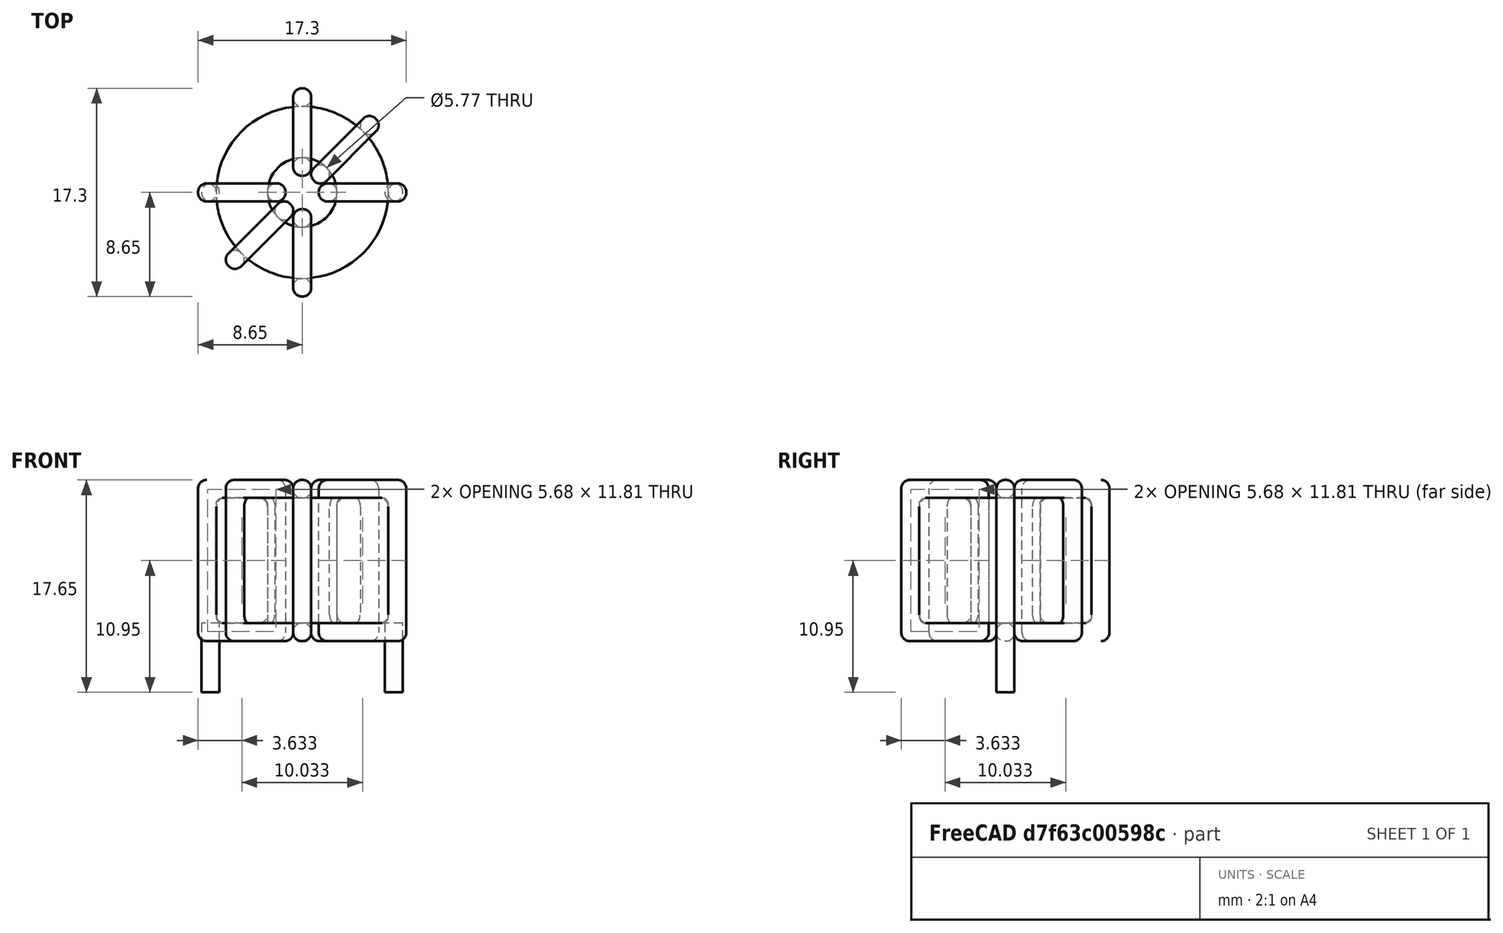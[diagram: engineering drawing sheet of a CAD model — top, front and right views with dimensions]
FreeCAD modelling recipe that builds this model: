
FCSTD DOCUMENT  (FreeCAD 0.16R6703 (Git))
Label: L_Toroid_Horizontal_D17.3mm_P15.24mm_Bourns_2000series
License: All rights reserved
LicenseURL: http://en.wikipedia.org/wiki/All_rights_reserved
objects: Sketcher::SketchObject×6, PartDesign::Pad×6, PartDesign::Fillet×5, Spreadsheet::Sheet×1
note: 23 computed .brp shape members not serialized (recipe doc carries the construction recipe); baked Part::Feature solids carry a one-line shape summary decoded from their .brp

FEATURE [Spreadsheet::Sheet] Spreadsheet  label="dimensions"
  cells = A1=Wx; B1(Wx)=17.3; C1(WW)=5.766666666666667; D1=17.3; A2=Wy; B2(Wy)=17.3; D2=17.3; A3=RM; B3(RMx)=15.24; C3(RMy)=0; A4=d_wire; B4(d_wire)=1.5; A5=H; B5(H)=10.4; A6=offsetx; B6(offsetx)=1.03
FEATURE [Sketcher::SketchObject] Sketch
  Placement = pos=(0,0,2) rot=(0,0,1;0rad)
  expr: Placement.Base.z = 0.5 + Spreadsheet.d_wire
  expr: Constraints[0] = Spreadsheet.Wx / 2 - Spreadsheet.d_wire
  expr: Constraints[4] = Spreadsheet.WW / 2
  expr: Constraints[2] = Spreadsheet.RMy / 2
  expr: Constraints[1] = Spreadsheet.RMx / 2
  sketch-geometry (2):
    g0: Circle CenterX=7.62 CenterY=0 CenterZ=0 NormalX=0 NormalY=0 NormalZ=1 Radius=7.15
    g1: Circle CenterX=7.62 CenterY=0 CenterZ=0 NormalX=0 NormalY=0 NormalZ=1 Radius=2.88333
  constraints (5):
    c: Radius(g0) = 7.15
    c: DistanceX(g-1,g0) = 7.62
    c: DistanceY(g-1,g0) = 0
    c: Coincident(g1,g0)
    c: Radius(g1) = 2.88333
FEATURE [PartDesign::Pad] Pad
  Length = 10.4
  Length2 = 100
  Placement = pos=(0,0,2) rot=(0,0,1;0rad)
  Sketch = -> Sketch
  Type = 0
  expr: Length = Spreadsheet.H
FEATURE [Sketcher::SketchObject] Sketch001
  Placement = pos=(0,0,1.25) rot=(0,0,1;0rad)
  expr: Placement.Base.z = 0.5 + Spreadsheet.d_wire * 0.5
  expr: Constraints[4] = Spreadsheet.RMx
  expr: Constraints[2] = Spreadsheet.RMy
  expr: Constraints[1] = Spreadsheet.d_wire / 2
  sketch-geometry (2):
    g0: Circle CenterX=0 CenterY=0 CenterZ=0 NormalX=0 NormalY=0 NormalZ=1 Radius=0.75
    g1: Circle CenterX=15.24 CenterY=0 CenterZ=0 NormalX=0 NormalY=0 NormalZ=1 Radius=0.75
  constraints (5):
    c: Equal(g0,g1)
    c: Radius(g0) = 0.75
    c: DistanceY(g-1,g1) = 0
    c: Coincident(g0,g-1)
    c: DistanceX(g-1,g1) = 15.24
FEATURE [PartDesign::Pad] Pad001
  Length = 0.75
  Length2 = 5
  Placement = pos=(0,0,1.25) rot=(0,0,1;0rad)
  Reversed = true
  Sketch = -> Sketch001
  Type = 4
  expr: Length2 = 3.5 + Spreadsheet.d_wire
  expr: Length = Spreadsheet.d_wire / 2
FEATURE [PartDesign::Fillet] Fillet
  Base = -> Pad [Edge6,Edge3,Edge2]
  Placement = pos=(0,0,2) rot=(0,0,1;0rad)
  Radius = 0.5
FEATURE [Sketcher::SketchObject] Sketch003
  Placement = pos=(7.62,0,0) rot=(1,0,0;1.5708rad)
  expr: Placement.Base.x = Spreadsheet.RMx / 2
  expr: Constraints[49] = Spreadsheet.Wx - Spreadsheet.d_wire * 2
  expr: Constraints[44] = Spreadsheet.d_wire
  expr: Constraints[23] = Spreadsheet.H
  expr: Constraints[22] = Spreadsheet.Wx / 2 - Spreadsheet.d_wire
  expr: Placement.Base.y = Spreadsheet.RMy / 2
  expr: Constraints[21] = (Spreadsheet.Wx - Spreadsheet.WW) / 2 - Spreadsheet.d_wire
  expr: Constraints[19] = Spreadsheet.d_wire
  expr: Constraints[17] = Spreadsheet.d_wire
  expr: Constraints[18] = Spreadsheet.d_wire
  expr: Constraints[16] = Spreadsheet.d_wire
  sketch-geometry (16):
    g0: LineSegment StartX=-1.38333 StartY=0.5 StartZ=0 EndX=-8.65 EndY=0.5 EndZ=0
    g1: LineSegment StartX=-8.65 StartY=0.5 StartZ=0 EndX=-8.65 EndY=13.9 EndZ=0
    g2: LineSegment StartX=-8.65 StartY=13.9 StartZ=0 EndX=-1.38333 EndY=13.9 EndZ=0
    g3: LineSegment StartX=-1.38333 StartY=13.9 StartZ=0 EndX=-1.38333 EndY=0.5 EndZ=0
    g4: LineSegment StartX=-7.15 StartY=12.4 StartZ=0 EndX=-2.88333 EndY=12.4 EndZ=0
    g5: LineSegment StartX=-2.88333 StartY=12.4 StartZ=0 EndX=-2.88333 EndY=2 EndZ=0
    g6: LineSegment StartX=-2.88333 StartY=2 StartZ=0 EndX=-7.15 EndY=2 EndZ=0
    g7: LineSegment StartX=-7.15 StartY=2 StartZ=0 EndX=-7.15 EndY=12.4 EndZ=0
    g8: LineSegment StartX=1.38333 StartY=13.9 StartZ=0 EndX=8.65 EndY=13.9 EndZ=0
    g9: LineSegment StartX=8.65 StartY=13.9 StartZ=0 EndX=8.65 EndY=0.5 EndZ=0
    g10: LineSegment StartX=8.65 StartY=0.5 StartZ=0 EndX=1.38333 EndY=0.5 EndZ=0
    g11: LineSegment StartX=1.38333 StartY=0.5 StartZ=0 EndX=1.38333 EndY=13.9 EndZ=0
    g12: LineSegment StartX=2.88333 StartY=12.4 StartZ=0 EndX=7.15 EndY=12.4 EndZ=0
    g13: LineSegment StartX=7.15 StartY=12.4 StartZ=0 EndX=7.15 EndY=2 EndZ=0
    g14: LineSegment StartX=7.15 StartY=2 StartZ=0 EndX=2.88333 EndY=2 EndZ=0
    g15: LineSegment StartX=2.88333 StartY=2 StartZ=0 EndX=2.88333 EndY=12.4 EndZ=0
  constraints (50):
    c: Horizontal(g0)
    c: Coincident(g1,g0)
    c: Vertical(g1)
    c: Coincident(g2,g1)
    c: Horizontal(g2)
    c: Coincident(g3,g2)
    c: Coincident(g3,g0)
    c: Vertical(g3)
    c: Coincident(g4,g5)
    c: Coincident(g5,g6)
    c: Coincident(g6,g7)
    c: Coincident(g7,g4)
    c: Horizontal(g4)
    c: Horizontal(g6)
    c: Vertical(g5)
    c: Vertical(g7)
    c: DistanceX(g1,g4) = 1.5
    c: DistanceY(g4,g1) = 1.5
    c: DistanceX(g5,g0) = 1.5
    c: DistanceY(g0,g5) = 1.5
    c: DistanceY(g-1,g0) = 0.5
    c: DistanceX(g6,g6) = 4.26667
    c: DistanceX(g6,g-1) = 7.15
    c: DistanceY(g7,g7) = 10.4
    c: Coincident(g8,g9)
    c: Coincident(g9,g10)
    c: Coincident(g10,g11)
    c: Coincident(g11,g8)
    c: Horizontal(g8)
    c: Horizontal(g10)
    c: Vertical(g9)
    c: Vertical(g11)
    c: Coincident(g12,g13)
    c: Coincident(g13,g14)
    c: Coincident(g14,g15)
    c: Coincident(g15,g12)
    c: Horizontal(g12)
    c: Horizontal(g14)
    c: Vertical(g13)
    c: Vertical(g15)
    c: DistanceY(g8,g2) = 0
    c: DistanceY(g10,g0) = 0
    c: DistanceY(g14,g5) = 0
    c: DistanceY(g12,g4) = 0
    c: DistanceX(g8,g12) = 1.5
    c: Equal(g8,g2)
    c: Equal(g12,g4)
    c: Equal(g9,g1)
    c: Equal(g13,g7)
    c: DistanceX(g4,g12) = 14.3
FEATURE [PartDesign::Pad] Pad002
  Length = 1.5
  Length2 = 100
  Midplane = true
  Placement = pos=(7.62,0,0) rot=(1,0,0;1.5708rad)
  Sketch = -> Sketch003
  Type = 0
  expr: Length = Spreadsheet.d_wire
FEATURE [PartDesign::Fillet] Fillet001
  Base = -> Pad002 [Edge38,Edge41,Edge42,Edge43,Edge29,Edge32,Edge33,Edge34,Edge25,Edge35,Edge36,Edge13,Edge14,Edge15,Edge16,Edge17,Edge18,Edge19,Edge1,Edge2,Edge3,Edge4,Edge5,Edge6,Edge7,Edge37,Edge39,Edge40,Edge20,Edge23,Edge24,Edge21,Edge22,Edge8,Edge9,Edge10,Edge11,Edge12,Edge26,Edge27,+8 more]
  Placement = pos=(7.62,0,0) rot=(1,0,0;1.5708rad)
  Radius = 0.705
  expr: Radius = Spreadsheet.d_wire * 0.47
FEATURE [Sketcher::SketchObject] Sketch004
  Placement = pos=(7.62,0,0) rot=(0.862856,0.357407,0.357407;1.71777rad)
  expr: Placement.Base.x = Spreadsheet.RMx / 2
  expr: Constraints[49] = Spreadsheet.Wx - 2 * Spreadsheet.d_wire
  expr: Constraints[44] = Spreadsheet.d_wire
  expr: Constraints[23] = Spreadsheet.H
  expr: Constraints[22] = Spreadsheet.Wx / 2 - Spreadsheet.d_wire
  expr: Placement.Base.y = Spreadsheet.RMy / 2
  expr: Constraints[21] = (Spreadsheet.Wx - Spreadsheet.WW) / 2 - Spreadsheet.d_wire
  expr: Constraints[19] = Spreadsheet.d_wire
  expr: Constraints[17] = Spreadsheet.d_wire
  expr: Constraints[18] = Spreadsheet.d_wire
  expr: Constraints[16] = Spreadsheet.d_wire
  sketch-geometry (16):
    g0: LineSegment StartX=-1.38333 StartY=0.5 StartZ=0 EndX=-8.65 EndY=0.5 EndZ=0
    g1: LineSegment StartX=-8.65 StartY=0.5 StartZ=0 EndX=-8.65 EndY=13.9 EndZ=0
    g2: LineSegment StartX=-8.65 StartY=13.9 StartZ=0 EndX=-1.38333 EndY=13.9 EndZ=0
    g3: LineSegment StartX=-1.38333 StartY=13.9 StartZ=0 EndX=-1.38333 EndY=0.5 EndZ=0
    g4: LineSegment StartX=-7.15 StartY=12.4 StartZ=0 EndX=-2.88333 EndY=12.4 EndZ=0
    g5: LineSegment StartX=-2.88333 StartY=12.4 StartZ=0 EndX=-2.88333 EndY=2 EndZ=0
    g6: LineSegment StartX=-2.88333 StartY=2 StartZ=0 EndX=-7.15 EndY=2 EndZ=0
    g7: LineSegment StartX=-7.15 StartY=2 StartZ=0 EndX=-7.15 EndY=12.4 EndZ=0
    g8: LineSegment StartX=1.38333 StartY=13.9 StartZ=0 EndX=8.65 EndY=13.9 EndZ=0
    g9: LineSegment StartX=8.65 StartY=13.9 StartZ=0 EndX=8.65 EndY=0.5 EndZ=0
    g10: LineSegment StartX=8.65 StartY=0.5 StartZ=0 EndX=1.38333 EndY=0.5 EndZ=0
    g11: LineSegment StartX=1.38333 StartY=0.5 StartZ=0 EndX=1.38333 EndY=13.9 EndZ=0
    g12: LineSegment StartX=2.88333 StartY=12.4 StartZ=0 EndX=7.15 EndY=12.4 EndZ=0
    g13: LineSegment StartX=7.15 StartY=12.4 StartZ=0 EndX=7.15 EndY=2 EndZ=0
    g14: LineSegment StartX=7.15 StartY=2 StartZ=0 EndX=2.88333 EndY=2 EndZ=0
    g15: LineSegment StartX=2.88333 StartY=2 StartZ=0 EndX=2.88333 EndY=12.4 EndZ=0
  constraints (50):
    c: Horizontal(g0)
    c: Coincident(g1,g0)
    c: Vertical(g1)
    c: Coincident(g2,g1)
    c: Horizontal(g2)
    c: Coincident(g3,g2)
    c: Coincident(g3,g0)
    c: Vertical(g3)
    c: Coincident(g4,g5)
    c: Coincident(g5,g6)
    c: Coincident(g6,g7)
    c: Coincident(g7,g4)
    c: Horizontal(g4)
    c: Horizontal(g6)
    c: Vertical(g5)
    c: Vertical(g7)
    c: DistanceX(g1,g4) = 1.5
    c: DistanceY(g4,g1) = 1.5
    c: DistanceX(g5,g0) = 1.5
    c: DistanceY(g0,g5) = 1.5
    c: DistanceY(g-1,g0) = 0.5
    c: DistanceX(g6,g6) = 4.26667
    c: DistanceX(g6,g-1) = 7.15
    c: DistanceY(g7,g7) = 10.4
    c: Coincident(g8,g9)
    c: Coincident(g9,g10)
    c: Coincident(g10,g11)
    c: Coincident(g11,g8)
    c: Horizontal(g8)
    c: Horizontal(g10)
    c: Vertical(g9)
    c: Vertical(g11)
    c: Coincident(g12,g13)
    c: Coincident(g13,g14)
    c: Coincident(g14,g15)
    c: Coincident(g15,g12)
    c: Horizontal(g12)
    c: Horizontal(g14)
    c: Vertical(g13)
    c: Vertical(g15)
    c: DistanceY(g8,g2) = 0
    c: DistanceY(g10,g0) = 0
    c: DistanceY(g14,g5) = 0
    c: DistanceY(g12,g4) = 0
    c: DistanceX(g8,g12) = 1.5
    c: Equal(g8,g2)
    c: Equal(g12,g4)
    c: Equal(g9,g1)
    c: Equal(g13,g7)
    c: DistanceX(g4,g12) = 14.3
FEATURE [PartDesign::Pad] Pad003
  Length = 1.5
  Length2 = 100
  Midplane = true
  Placement = pos=(7.62,0,0) rot=(0.862856,0.357407,0.357407;1.71777rad)
  Sketch = -> Sketch004
  Type = 0
  expr: Length = Spreadsheet.d_wire
FEATURE [PartDesign::Fillet] Fillet002
  Base = -> Pad003 [Edge38,Edge41,Edge42,Edge43,Edge29,Edge32,Edge33,Edge34,Edge25,Edge35,Edge36,Edge13,Edge14,Edge15,Edge16,Edge17,Edge18,Edge19,Edge1,Edge2,Edge3,Edge4,Edge5,Edge6,Edge7,Edge37,Edge39,Edge40,Edge20,Edge23,Edge24,Edge21,Edge22,Edge8,Edge9,Edge10,Edge11,Edge12,Edge26,Edge27,+8 more]
  Placement = pos=(7.62,0,0) rot=(0.862856,0.357407,0.357407;1.71777rad)
  Radius = 0.705
  expr: Radius = Spreadsheet.d_wire * 0.47
FEATURE [Sketcher::SketchObject] Sketch005
  Placement = pos=(7.62,0,0) rot=(0.862856,-0.357407,-0.357407;1.71777rad)
  expr: Placement.Base.x = Spreadsheet.RMx / 2
  expr: Constraints[49] = Spreadsheet.Wx - 2 * Spreadsheet.d_wire
  expr: Constraints[44] = Spreadsheet.d_wire
  expr: Constraints[23] = Spreadsheet.H
  expr: Constraints[22] = Spreadsheet.Wx / 2 - Spreadsheet.d_wire
  expr: Placement.Base.y = Spreadsheet.RMy / 2
  expr: Constraints[21] = (Spreadsheet.Wx - Spreadsheet.WW) / 2 - Spreadsheet.d_wire
  expr: Constraints[19] = Spreadsheet.d_wire
  expr: Constraints[17] = Spreadsheet.d_wire
  expr: Constraints[18] = Spreadsheet.d_wire
  expr: Constraints[16] = Spreadsheet.d_wire
  sketch-geometry (16):
    g0: LineSegment StartX=-1.38333 StartY=0.5 StartZ=0 EndX=-8.65 EndY=0.5 EndZ=0
    g1: LineSegment StartX=-8.65 StartY=0.5 StartZ=0 EndX=-8.65 EndY=13.9 EndZ=0
    g2: LineSegment StartX=-8.65 StartY=13.9 StartZ=0 EndX=-1.38333 EndY=13.9 EndZ=0
    g3: LineSegment StartX=-1.38333 StartY=13.9 StartZ=0 EndX=-1.38333 EndY=0.5 EndZ=0
    g4: LineSegment StartX=-7.15 StartY=12.4 StartZ=0 EndX=-2.88333 EndY=12.4 EndZ=0
    g5: LineSegment StartX=-2.88333 StartY=12.4 StartZ=0 EndX=-2.88333 EndY=2 EndZ=0
    g6: LineSegment StartX=-2.88333 StartY=2 StartZ=0 EndX=-7.15 EndY=2 EndZ=0
    g7: LineSegment StartX=-7.15 StartY=2 StartZ=0 EndX=-7.15 EndY=12.4 EndZ=0
    g8: LineSegment StartX=1.38333 StartY=13.9 StartZ=0 EndX=8.65 EndY=13.9 EndZ=0
    g9: LineSegment StartX=8.65 StartY=13.9 StartZ=0 EndX=8.65 EndY=0.5 EndZ=0
    g10: LineSegment StartX=8.65 StartY=0.5 StartZ=0 EndX=1.38333 EndY=0.5 EndZ=0
    g11: LineSegment StartX=1.38333 StartY=0.5 StartZ=0 EndX=1.38333 EndY=13.9 EndZ=0
    g12: LineSegment StartX=2.88333 StartY=12.4 StartZ=0 EndX=7.15 EndY=12.4 EndZ=0
    g13: LineSegment StartX=7.15 StartY=12.4 StartZ=0 EndX=7.15 EndY=2 EndZ=0
    g14: LineSegment StartX=7.15 StartY=2 StartZ=0 EndX=2.88333 EndY=2 EndZ=0
    g15: LineSegment StartX=2.88333 StartY=2 StartZ=0 EndX=2.88333 EndY=12.4 EndZ=0
  constraints (50):
    c: Horizontal(g0)
    c: Coincident(g1,g0)
    c: Vertical(g1)
    c: Coincident(g2,g1)
    c: Horizontal(g2)
    c: Coincident(g3,g2)
    c: Coincident(g3,g0)
    c: Vertical(g3)
    c: Coincident(g4,g5)
    c: Coincident(g5,g6)
    c: Coincident(g6,g7)
    c: Coincident(g7,g4)
    c: Horizontal(g4)
    c: Horizontal(g6)
    c: Vertical(g5)
    c: Vertical(g7)
    c: DistanceX(g1,g4) = 1.5
    c: DistanceY(g4,g1) = 1.5
    c: DistanceX(g5,g0) = 1.5
    c: DistanceY(g0,g5) = 1.5
    c: DistanceY(g-1,g0) = 0.5
    c: DistanceX(g6,g6) = 4.26667
    c: DistanceX(g6,g-1) = 7.15
    c: DistanceY(g7,g7) = 10.4
    c: Coincident(g8,g9)
    c: Coincident(g9,g10)
    c: Coincident(g10,g11)
    c: Coincident(g11,g8)
    c: Horizontal(g8)
    c: Horizontal(g10)
    c: Vertical(g9)
    c: Vertical(g11)
    c: Coincident(g12,g13)
    c: Coincident(g13,g14)
    c: Coincident(g14,g15)
    c: Coincident(g15,g12)
    c: Horizontal(g12)
    c: Horizontal(g14)
    c: Vertical(g13)
    c: Vertical(g15)
    c: DistanceY(g8,g2) = 0
    c: DistanceY(g10,g0) = 0
    c: DistanceY(g14,g5) = 0
    c: DistanceY(g12,g4) = 0
    c: DistanceX(g8,g12) = 1.5
    c: Equal(g8,g2)
    c: Equal(g12,g4)
    c: Equal(g9,g1)
    c: Equal(g13,g7)
    c: DistanceX(g4,g12) = 14.3
FEATURE [PartDesign::Pad] Pad004
  Length = 1.5
  Length2 = 100
  Midplane = true
  Placement = pos=(7.62,0,0) rot=(0.862856,-0.357407,-0.357407;1.71777rad)
  Sketch = -> Sketch005
  Type = 0
  expr: Length = Spreadsheet.d_wire
FEATURE [PartDesign::Fillet] Fillet003
  Base = -> Pad004 [Edge38,Edge41,Edge42,Edge43,Edge29,Edge32,Edge33,Edge34,Edge25,Edge35,Edge36,Edge13,Edge14,Edge15,Edge16,Edge17,Edge18,Edge19,Edge1,Edge2,Edge3,Edge4,Edge5,Edge6,Edge7,Edge37,Edge39,Edge40,Edge20,Edge23,Edge24,Edge21,Edge22,Edge8,Edge9,Edge10,Edge11,Edge12,Edge26,Edge27,+8 more]
  Placement = pos=(7.62,0,0) rot=(0.862856,-0.357407,-0.357407;1.71777rad)
  Radius = 0.705
  expr: Radius = Spreadsheet.d_wire * 0.47
FEATURE [Sketcher::SketchObject] Sketch006
  Placement = pos=(7.62,0,0) rot=(0.57735,0.57735,0.57735;2.0944rad)
  expr: Placement.Base.x = Spreadsheet.RMx / 2
  expr: Constraints[49] = Spreadsheet.Wx - Spreadsheet.d_wire * 2
  expr: Constraints[44] = Spreadsheet.d_wire
  expr: Constraints[23] = Spreadsheet.H
  expr: Constraints[22] = Spreadsheet.Wx / 2 - Spreadsheet.d_wire
  expr: Placement.Base.y = Spreadsheet.RMy / 2
  expr: Constraints[21] = (Spreadsheet.Wx - Spreadsheet.WW) / 2 - Spreadsheet.d_wire
  expr: Constraints[19] = Spreadsheet.d_wire
  expr: Constraints[17] = Spreadsheet.d_wire
  expr: Constraints[18] = Spreadsheet.d_wire
  expr: Constraints[16] = Spreadsheet.d_wire
  sketch-geometry (16):
    g0: LineSegment StartX=-1.38333 StartY=0.5 StartZ=0 EndX=-8.65 EndY=0.5 EndZ=0
    g1: LineSegment StartX=-8.65 StartY=0.5 StartZ=0 EndX=-8.65 EndY=13.9 EndZ=0
    g2: LineSegment StartX=-8.65 StartY=13.9 StartZ=0 EndX=-1.38333 EndY=13.9 EndZ=0
    g3: LineSegment StartX=-1.38333 StartY=13.9 StartZ=0 EndX=-1.38333 EndY=0.5 EndZ=0
    g4: LineSegment StartX=-7.15 StartY=12.4 StartZ=0 EndX=-2.88333 EndY=12.4 EndZ=0
    g5: LineSegment StartX=-2.88333 StartY=12.4 StartZ=0 EndX=-2.88333 EndY=2 EndZ=0
    g6: LineSegment StartX=-2.88333 StartY=2 StartZ=0 EndX=-7.15 EndY=2 EndZ=0
    g7: LineSegment StartX=-7.15 StartY=2 StartZ=0 EndX=-7.15 EndY=12.4 EndZ=0
    g8: LineSegment StartX=1.38333 StartY=13.9 StartZ=0 EndX=8.65 EndY=13.9 EndZ=0
    g9: LineSegment StartX=8.65 StartY=13.9 StartZ=0 EndX=8.65 EndY=0.5 EndZ=0
    g10: LineSegment StartX=8.65 StartY=0.5 StartZ=0 EndX=1.38333 EndY=0.5 EndZ=0
    g11: LineSegment StartX=1.38333 StartY=0.5 StartZ=0 EndX=1.38333 EndY=13.9 EndZ=0
    g12: LineSegment StartX=2.88333 StartY=12.4 StartZ=0 EndX=7.15 EndY=12.4 EndZ=0
    g13: LineSegment StartX=7.15 StartY=12.4 StartZ=0 EndX=7.15 EndY=2 EndZ=0
    g14: LineSegment StartX=7.15 StartY=2 StartZ=0 EndX=2.88333 EndY=2 EndZ=0
    g15: LineSegment StartX=2.88333 StartY=2 StartZ=0 EndX=2.88333 EndY=12.4 EndZ=0
  constraints (50):
    c: Horizontal(g0)
    c: Coincident(g1,g0)
    c: Vertical(g1)
    c: Coincident(g2,g1)
    c: Horizontal(g2)
    c: Coincident(g3,g2)
    c: Coincident(g3,g0)
    c: Vertical(g3)
    c: Coincident(g4,g5)
    c: Coincident(g5,g6)
    c: Coincident(g6,g7)
    c: Coincident(g7,g4)
    c: Horizontal(g4)
    c: Horizontal(g6)
    c: Vertical(g5)
    c: Vertical(g7)
    c: DistanceX(g1,g4) = 1.5
    c: DistanceY(g4,g1) = 1.5
    c: DistanceX(g5,g0) = 1.5
    c: DistanceY(g0,g5) = 1.5
    c: DistanceY(g-1,g0) = 0.5
    c: DistanceX(g6,g6) = 4.26667
    c: DistanceX(g6,g-1) = 7.15
    c: DistanceY(g7,g7) = 10.4
    c: Coincident(g8,g9)
    c: Coincident(g9,g10)
    c: Coincident(g10,g11)
    c: Coincident(g11,g8)
    c: Horizontal(g8)
    c: Horizontal(g10)
    c: Vertical(g9)
    c: Vertical(g11)
    c: Coincident(g12,g13)
    c: Coincident(g13,g14)
    c: Coincident(g14,g15)
    c: Coincident(g15,g12)
    c: Horizontal(g12)
    c: Horizontal(g14)
    c: Vertical(g13)
    c: Vertical(g15)
    c: DistanceY(g8,g2) = 0
    c: DistanceY(g10,g0) = 0
    c: DistanceY(g14,g5) = 0
    c: DistanceY(g12,g4) = 0
    c: DistanceX(g8,g12) = 1.5
    c: Equal(g8,g2)
    c: Equal(g12,g4)
    c: Equal(g9,g1)
    c: Equal(g13,g7)
    c: DistanceX(g4,g12) = 14.3
FEATURE [PartDesign::Pad] Pad005
  Length = 1.5
  Length2 = 100
  Midplane = true
  Placement = pos=(7.62,0,0) rot=(0.57735,0.57735,0.57735;2.0944rad)
  Sketch = -> Sketch006
  Type = 0
  expr: Length = Spreadsheet.d_wire
FEATURE [PartDesign::Fillet] Fillet004
  Base = -> Pad005 [Edge38,Edge41,Edge42,Edge43,Edge29,Edge32,Edge33,Edge34,Edge25,Edge35,Edge36,Edge13,Edge14,Edge15,Edge16,Edge17,Edge18,Edge19,Edge1,Edge2,Edge3,Edge4,Edge5,Edge6,Edge7,Edge37,Edge39,Edge40,Edge20,Edge23,Edge24,Edge21,Edge22,Edge8,Edge9,Edge10,Edge11,Edge12,Edge26,Edge27,+8 more]
  Placement = pos=(7.62,0,0) rot=(0.57735,0.57735,0.57735;2.0944rad)
  Radius = 0.705
  expr: Radius = Spreadsheet.d_wire * 0.47
